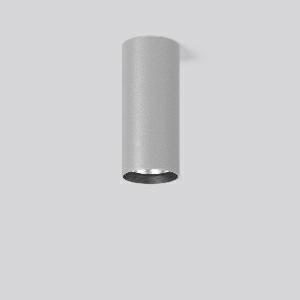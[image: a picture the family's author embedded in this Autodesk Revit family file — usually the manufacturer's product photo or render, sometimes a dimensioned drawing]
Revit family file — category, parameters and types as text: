
# Revit family: heledon_mini_a_931210_004_2_76_ea2f
name_source: partatom
category: Lighting Fixtures
units: mm (PartAtom-declared; Revit-internal decimal feet)

## family parameters
Cut with Voids When Loaded = No
Host = Face
Light Source = No
Part Type = Normal
Room Calculation Point = No
Round Connector Dimension = Use Diameter
Shared = No

## types (1)
- HELEDON mini A (1 x LED Modul 927, 3500 lm, 2700)
    Apparent Load = 29 VA
    Approval mark = CE
    CIE Flux Codes = 95 99 100 100 100
    Color Rendering = 92
    Color Temperature = 2700
    Default Elevation = 1800 mm
    Description = Series: HELEDON mini
Cylindrical surface-mounted downlight. Housing: die-cast aluminium, powder-coated. Internal ceiling frame polycarbonate with bayonet mounting. Black plastic ring and recessed LED to prevent glare from the side. Optical assembly with reflector made of MIRO-Silver with 98% total light reflection for outstanding efficiency - can be changed without tools. Best colour rendering index Ra>90. Suitable for Ceiling mounting. Easy installation with a separate ceiling frame with bayonet mounting and plug connection. Driver integrated. Connected via plug-in connector. High quality converter without flickering and stroboscopic effect. The following accessories can be mounted without use of tools: interchangeable lenses, decorative glasses, honeycomb louvre, clear and frosted diffusers, white interchangeable plastic ring. 
Colour: silver
Diameter: 87 mm
Height: 197 mm
Lamp: LED
Socket: without socket
Colour temperature: 2700K
Colour rendering index (CRI): 92
System power: 29 W
Rated luminous flux: 3500 lm
Luminous efficiency: 121 lm/W
Control gear: Converter, dimmable, DALI
Protection class: I
Type of protection: IP 20
    Height = 197 mm
    Lamp = 1 x LED Modul 927
    Lamp Light Flux = 3500 lm
    Lamp count = 1
    Length = 87 mm
    Lifetime = 50000 h
    Luminous efficacy = 121 lm/W
    Manufacturer = RZB
    ModVariant = No
    Model = 931210.004.2.76
    Mounting Place = Ceiling
    Mounting Type = Surface mounted
    Number of Poles = 1
    OnlyDefault = Yes
    Power Factor = 1
    Product Name = HELEDON mini A
    Product group = Surface mounted downlights
    ProductGroupID = 302
    Protection Class = Protection class I
    Protection Degree = IP 20
    RLX_Detail_Level = 1
    RLX_Emergency_Light_Flux = 0 lm
    RLX_Emergency_Type = 0
    RLX_Emergency_Type_DB = No
    RlxData = <blob elided: 107085 chars, md5=a2628144>
    Socket = socket
    Standby Power = 0 W
    System Light Flux = 3500 lm
    System Power = 29 W
    Type Comments = Product without accessories
    Type Image = 931188.004.jpg
    URL = http://relux.com
    VarID = ---
    Voltage = 230 V
    Voltage Range = 220-240 V
    Weight = 0.00 kg
    Width = 0 mm  [stored 0 ft]

note: [stored X ft] marks values corroborated as IEEE doubles in the binary element streams (Revit-internal decimal feet)

## geometry (parser evidence)
native form markers: Blend x4, Sweep x10
no freeform markers — native parametric forms only
